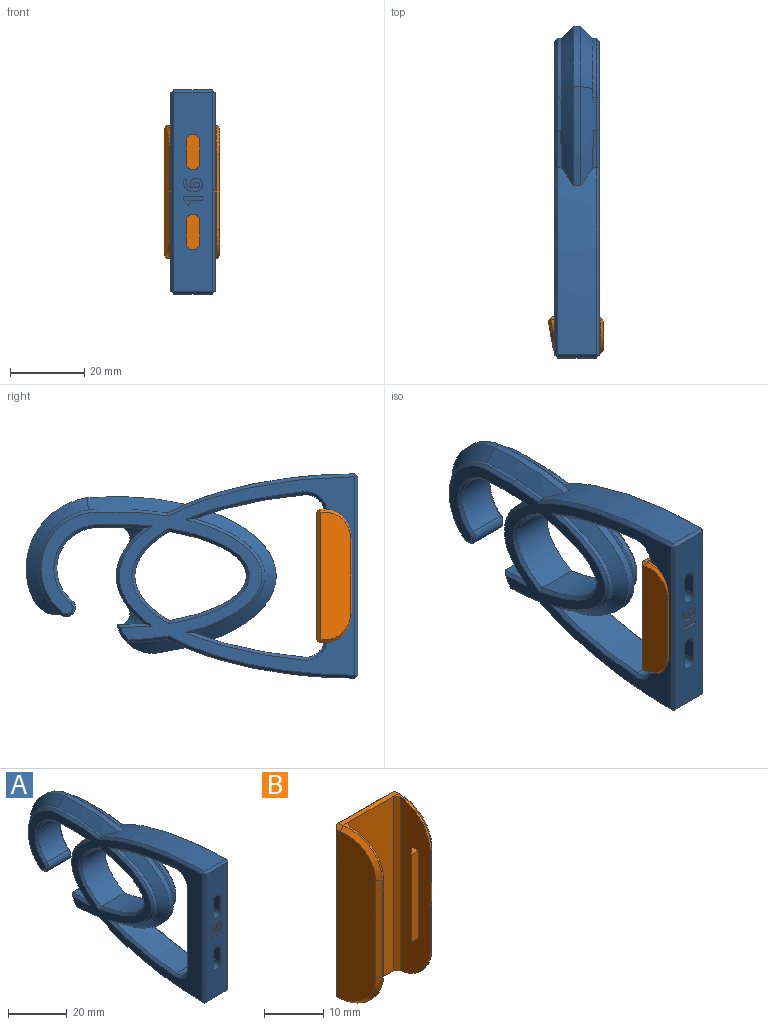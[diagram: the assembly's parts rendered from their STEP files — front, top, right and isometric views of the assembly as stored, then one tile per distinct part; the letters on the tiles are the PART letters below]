
ASSEMBLY  parts=2 mates=1
PART A: 167 faces, bbox 13x92.1x56.1 mm
  f0: plane 53.4x10.4mm, normal (0,-1,0), area 475.3mm2, adj f27,f28,f29,f30,f31,f32,f33,f34
  f1: cylinder r=16mm len=28.43mm, axis (-1,0,0), area 47.1mm2, adj f11,f13,f65,f66,f70,f76,f105
  f2: extruded ~10.08x1.04mm, area 9.1mm2, adj f13,f15,f70,f101
  f3: extruded ~10.91x4.2mm, area 19mm2, adj f16,f18,f62,f63,f100
  f4: extruded ~30.7x18.87mm, area 61.6mm2, adj f7,f10,f48,f114
  f5: plane 33.72x10.4mm, normal (0,1,0), area 111.2mm2, adj f8,f9,f35,f37,f38,f39,f40,f41
  f6: extruded ~24x11.2mm, area 354.4mm2, adj f24,f25,f122
  f7: extruded ~29.4x10.4mm, area 288mm2, adj f4,f8,f22,f47,f48,f49,f115,f119
  f8: cylinder r=5mm len=10.4mm, axis (-1,0,0), area 81.4mm2, adj f5,f7,f43,f113,f121
  f9: cylinder r=5mm len=10.4mm, axis (-1,0,0), area 81.4mm2, adj f5,f10,f36,f110,f118
  f10: extruded ~29.4x10.4mm, area 288mm2, adj f4,f9,f22,f47,f48,f49,f112,f116
  f11: cylinder r=2.5mm len=10.4mm, axis (-1,0,0), area 81.7mm2, adj f1,f12,f23,f72,f81,f107
  f12: cylinder r=16mm len=28.43mm, axis (-1,0,0), area 47.1mm2, adj f11,f13,f67,f68,f71,f77,f83
  f13: plane 10.41x8.77mm, normal (0,0,1), area 80.5mm2, adj f1,f2,f12,f14,f70,f71,f75,f85
  f14: extruded ~10.08x1.04mm, area 9.1mm2, adj f13,f15,f71,f87
  f15: extruded ~50.36x10.53mm, area 511.9mm2, adj f2,f14,f69,f70,f71,f90,f95,f99
  f16: extruded ~50.36x10.53mm, area 511.8mm2, adj f3,f17,f60,f62,f64,f88,f93,f98
  f17: extruded ~10.91x4.2mm, area 19mm2, adj f16,f18,f60,f61,f86
  f18: cylinder r=9.71mm len=10.76mm, axis (-1,0,0), area 76.6mm2, adj f3,f17,f19,f61,f63,f64,f84,f102
  f19: extruded ~10.4x7.29mm, area 38.9mm2, adj f18,f20,f55,f56,f57,f58,f59,f82
  f20: extruded ~25.66x10.4mm, area 250.9mm2, adj f19,f21,f50,f51,f52,f53,f54,f55
  f21: extruded ~13.86x10.4mm, area 107.3mm2, adj f20,f23,f50,f51,f52,f53,f54,f78
  f22: extruded ~30.7x18.87mm, area 61.6mm2, adj f7,f10,f47,f117
  f23: cylinder r=11mm len=19.46mm, axis (-1,0,0), area 267.4mm2, adj f11,f21,f79,f109
  f24: extruded ~24x20.76mm, area 570.7mm2, adj f6,f25,f123
  f25: plane 85.41x54.41mm, normal (1,0,0), area 1216.5mm2, adj f6,f24,f94,f98,f99,f100,f101,f102
  f26: plane 85.41x54.41mm, normal (-1,0,0), area 1177.9mm2, adj f78,f79,f80,f81,f82,f83,f84,f85
  f27: cylinder r=1.75mm len=6mm, axis (0,-1,0), area 33mm2, adj f0,f28,f30,f44
  f28: plane 6x6mm, normal (1,0,0), area 36mm2, adj f0,f27,f29,f42
  f29: cylinder r=1.75mm len=6mm, axis (0,-1,0), area 33mm2, adj f0,f28,f30,f41,f43,f45
  f30: plane 6x6mm, normal (-1,0,0), area 36mm2, adj f0,f27,f29,f46
  f31: plane 6x6mm, normal (-1,0,0), area 36mm2, adj f0,f32,f34,f40
  f32: cylinder r=1.75mm len=6mm, axis (0,-1,0), area 33mm2, adj f0,f31,f33,f35,f36,f38
  f33: plane 6x6mm, normal (1,0,0), area 36mm2, adj f0,f32,f34,f37
  f34: cylinder r=1.75mm len=6mm, axis (0,-1,0), area 33mm2, adj f0,f31,f33,f39
  f35: cone r=4.75mm half-angle=45deg, axis (0,1,0), area 9.8mm2, adj f5,f32,f36,f37
  f36: bspline ~7.18x3.11mm, area 20.9mm2, adj f9,f32,f35,f38
  f37: plane 6x3mm, normal (0.71,0.71,0), area 25.5mm2, adj f5,f33,f35,f39
  f38: cone r=4.75mm half-angle=45deg, axis (0,1,0), area 9.8mm2, adj f5,f32,f36,f40
  f39: cone r=4.75mm half-angle=45deg, axis (0,1,0), area 43.3mm2, adj f5,f34,f37,f40
  f40: plane 6x3mm, normal (-0.71,0.71,0), area 25.5mm2, adj f5,f31,f38,f39
  f41: cone r=4.75mm half-angle=45deg, axis (0,1,0), area 9.8mm2, adj f5,f29,f42,f43
  f42: plane 6x3mm, normal (0.71,0.71,0), area 25.5mm2, adj f5,f28,f41,f44
  f43: bspline ~7.18x3.11mm, area 20.9mm2, adj f8,f29,f41,f45
  f44: cone r=4.75mm half-angle=45deg, axis (0,1,0), area 43.3mm2, adj f5,f27,f42,f46
  f45: cone r=4.75mm half-angle=45deg, axis (0,1,0), area 9.8mm2, adj f5,f29,f43,f46
  f46: plane 6x3mm, normal (-0.71,0.71,0), area 25.5mm2, adj f5,f30,f44,f45
  f47: bspline ~40.67x32.57mm, area 230mm2, adj f7,f10,f22,f49
  f48: bspline ~40.67x32.57mm, area 230mm2, adj f4,f7,f10,f49
  f49: extruded ~34.16x17.06mm, area 102.3mm2, adj f7,f10,f47,f48
  f50: cone r=3mm half-angle=45deg, axis (1,0,0), area 12.9mm2, adj f20,f21,f51,f54
  f51: plane 0.41x0.27mm, normal (1,0,0), area 0.1mm2, adj f20,f21,f50
  f52: cone r=7mm half-angle=45deg, axis (-1,0,0), area 12.9mm2, adj f20,f21,f53,f54
  f53: plane 0.41x0.27mm, normal (-1,0,0), area 0.1mm2, adj f20,f21,f52
  f54: cylinder r=3mm len=4.8mm, axis (-1,0,0), area 13.2mm2, adj f20,f21,f50,f52
  f55: cone r=3mm half-angle=45deg, axis (1,0,0), area 12.9mm2, adj f19,f20,f56,f59
  f56: plane 0.41x0.27mm, normal (1,0,0), area 0.1mm2, adj f19,f20,f55
  f57: cone r=7mm half-angle=45deg, axis (-1,0,0), area 12.9mm2, adj f19,f20,f58,f59
  f58: plane 0.41x0.27mm, normal (-1,0,0), area 0.1mm2, adj f19,f20,f57
  f59: cylinder r=3mm len=4.8mm, axis (-1,0,0), area 13.2mm2, adj f19,f20,f55,f57
  f60: bspline ~14.46x6.99mm, area 25.7mm2, adj f16,f17,f61,f64
  f61: cone r=9.71mm half-angle=45deg, axis (1,0,0), area 18.1mm2, adj f17,f18,f60
  f62: bspline ~14.46x6.99mm, area 25.7mm2, adj f3,f16,f63,f64
  f63: cone r=5.71mm half-angle=45deg, axis (-1,0,0), area 18.1mm2, adj f3,f18,f62
  f64: extruded ~7.7x2mm, area 15.7mm2, adj f16,f18,f60,f62
  f65: cone r=15.27mm half-angle=45deg, axis (-1,0,0), area 153mm2, adj f1,f66,f70,f74
  f66: cone r=3mm half-angle=45deg, axis (-1,0,0), area 22.6mm2, adj f1,f65,f73,f76
  f67: cone r=19.27mm half-angle=45deg, axis (1,0,0), area 153mm2, adj f12,f68,f71,f74
  f68: cone r=7mm half-angle=45deg, axis (1,0,0), area 22.6mm2, adj f12,f67,f73,f77
  f69: extruded ~26.57x2.12mm, area 53.5mm2, adj f15,f70,f71,f74
  f70: bspline ~38.15x7.96mm, area 112.2mm2, adj f1,f2,f13,f15,f65,f69,f75
  f71: bspline ~38.15x7.96mm, area 112.2mm2, adj f12,f13,f14,f15,f67,f69,f75
  f72: plane 2x0.93mm, normal (0,0,-1), area 1.9mm2, adj f11,f73,f76,f77
  f73: cylinder r=7mm len=6.28mm, axis (-1,0,0), area 15.6mm2, adj f66,f68,f72,f74
  f74: cylinder r=19.27mm len=27.58mm, axis (-1,0,0), area 72.4mm2, adj f65,f67,f69,f73
  f75: extruded ~8.66x7.52mm, area 65.2mm2, adj f13,f70,f71
  f76: plane 0.95x0.83mm, normal (0.71,0,-0.71), area 0.5mm2, adj f1,f66,f72
  f77: plane 0.95x0.83mm, normal (-0.71,0,-0.71), area 0.5mm2, adj f12,f68,f72
  f78: bspline ~16.07x1.3mm, area 16.9mm2, adj f21,f26,f79,f80
  f79: cone r=11.8mm half-angle=45deg, axis (-1,0,0), area 30.2mm2, adj f23,f26,f78,f81
  f80: bspline ~30.07x11.02mm, area 36.3mm2, adj f20,f26,f78,f82
  f81: cone r=2.5mm half-angle=45deg, axis (1,0,0), area 7.5mm2, adj f11,f26,f79,f83
  f82: bspline ~10.35x1.36mm, area 8.9mm2, adj f19,f26,f80,f84
  f83: cone r=16mm half-angle=45deg, axis (1,0,0), area 43.4mm2, adj f12,f26,f81,f85
  f84: cone r=9.71mm half-angle=45deg, axis (1,0,0), area 5.4mm2, adj f18,f26,f82,f86
  f85: plane 8.76x0.8mm, normal (-0.71,0,0.71), area 9.9mm2, adj f13,f26,f83,f87
  f86: bspline ~11.21x1.9mm, area 12.3mm2, adj f17,f26,f84,f88
  f87: bspline ~10.39x1.87mm, area 11.6mm2, adj f14,f26,f85,f90
  f88: bspline ~55.49x12.73mm, area 58.6mm2, adj f16,f26,f86,f91
  f89: plane 53.4x0.8mm, normal (-0.71,-0.71,0), area 60.4mm2, adj f0,f26,f91,f92
  f90: bspline ~55.49x12.73mm, area 58.6mm2, adj f15,f26,f87,f92
  f91: plane 0.8x0.8mm, normal (-0.58,-0.58,-0.58), area 0.6mm2, adj f88,f89,f93
  f92: plane 0.8x0.8mm, normal (-0.58,-0.58,0.58), area 0.6mm2, adj f89,f90,f95
  f93: plane 10.4x0.8mm, normal (0,-0.71,-0.71), area 11.8mm2, adj f0,f16,f91,f96
  f94: plane 53.4x0.8mm, normal (0.71,-0.71,0), area 60.4mm2, adj f0,f25,f96,f97
  f95: plane 10.4x0.8mm, normal (0,-0.71,0.71), area 11.8mm2, adj f0,f15,f92,f97
  f96: plane 0.8x0.8mm, normal (0.58,-0.58,-0.58), area 0.6mm2, adj f93,f94,f98
  f97: plane 0.8x0.8mm, normal (0.58,-0.58,0.58), area 0.6mm2, adj f94,f95,f99
  f98: bspline ~55.49x12.73mm, area 58.6mm2, adj f16,f25,f96,f100
  f99: bspline ~55.49x12.73mm, area 58.6mm2, adj f15,f25,f97,f101
  f100: bspline ~11.21x1.9mm, area 12.3mm2, adj f3,f25,f98,f102
  f101: bspline ~10.39x1.87mm, area 11.6mm2, adj f2,f25,f99,f103
  f102: cone r=8.91mm half-angle=45deg, axis (-1,0,0), area 5.4mm2, adj f18,f25,f100,f104
  f103: plane 8.76x0.8mm, normal (0.71,0,0.71), area 9.9mm2, adj f13,f25,f101,f105
  f104: bspline ~9.42x1.3mm, area 8.9mm2, adj f19,f25,f102,f106
  f105: cone r=15.2mm half-angle=45deg, axis (-1,0,0), area 43.4mm2, adj f1,f25,f103,f107
  f106: bspline ~30.07x11.02mm, area 36.3mm2, adj f20,f25,f104,f108
  f107: cone r=1.7mm half-angle=45deg, axis (-1,0,0), area 7.5mm2, adj f11,f25,f105,f109
  f108: bspline ~16.07x1.3mm, area 16.9mm2, adj f21,f25,f106,f109
  f109: cone r=11mm half-angle=45deg, axis (1,0,0), area 30.2mm2, adj f23,f25,f107,f108
  f110: cone r=5mm half-angle=45deg, axis (1,0,0), area 10.2mm2, adj f9,f25,f111,f112
  f111: plane 33.72x0.8mm, normal (0.71,0.71,0), area 38.1mm2, adj f5,f25,f110,f113
  f112: bspline ~31.88x8.19mm, area 35.6mm2, adj f10,f25,f110,f114
  f113: cone r=5.8mm half-angle=45deg, axis (1,0,0), area 10.2mm2, adj f8,f25,f111,f115
  f114: bspline ~31.9x21.32mm, area 60mm2, adj f4,f25,f112,f115
  f115: bspline ~33.39x8.89mm, area 35.7mm2, adj f7,f25,f113,f114
  f116: bspline ~33.36x8.88mm, area 35.6mm2, adj f10,f26,f117,f118
  f117: bspline ~33.07x23.99mm, area 60mm2, adj f22,f26,f116,f119
  f118: cone r=5.8mm half-angle=45deg, axis (-1,0,0), area 10.2mm2, adj f9,f26,f116,f120
  f119: bspline ~33.39x8.89mm, area 35.7mm2, adj f7,f26,f117,f121
  f120: plane 33.72x0.8mm, normal (-0.71,0.71,0), area 38.1mm2, adj f5,f26,f118,f121
  f121: cone r=5mm half-angle=45deg, axis (-1,0,0), area 10.2mm2, adj f8,f26,f119,f120
  f122: bspline ~27.31x11.74mm, area 37.1mm2, adj f6,f26,f123
  f123: bspline ~26.44x24.47mm, area 59.3mm2, adj f24,f26,f122
  f124: cylinder r=1mm len=2mm, axis (1,0,0), area 6.3mm2, adj f25,f125,f127,f128
  f125: plane 18x2mm, normal (0,1,0), area 36mm2, adj f25,f124,f126,f128
  f126: cylinder r=1mm len=2mm, axis (1,0,0), area 6.3mm2, adj f25,f125,f127,f128
  f127: plane 18x2mm, normal (0,-1,0), area 36mm2, adj f25,f124,f126,f128
  f128: plane 20x2mm, normal (1,0,0), area 39.1mm2, adj f124,f125,f126,f127
  f129: extruded ~0.6x0.52mm, area 0.4mm2, adj f130,f153,f154,f166
  f130: extruded ~0.6x0.54mm, area 0.4mm2, adj f129,f131,f154,f166
  f131: extruded ~0.68x0.6mm, area 0.4mm2, adj f130,f132,f154,f166
  f132: extruded ~0.6x0.48mm, area 0.3mm2, adj f131,f133,f154,f166
  f133: extruded ~0.6x0.54mm, area 0.4mm2, adj f132,f134,f154,f166
  f134: extruded ~0.6x0.51mm, area 0.3mm2, adj f133,f135,f154,f166
  f135: extruded ~0.6x0.57mm, area 0.4mm2, adj f134,f153,f154,f166
  f136: extruded ~2.19x0.62mm, area 1.4mm2, adj f0,f137,f152,f154
  f137: extruded ~1.18x0.6mm, area 0.7mm2, adj f0,f136,f138,f154
  f138: extruded ~0.74x0.63mm, area 0.6mm2, adj f0,f137,f139,f154
  f139: extruded ~0.96x0.6mm, area 0.6mm2, adj f0,f138,f140,f154
  f140: extruded ~1.24x0.6mm, area 0.8mm2, adj f0,f139,f141,f154
  f141: extruded ~1.26x0.6mm, area 0.8mm2, adj f0,f140,f142,f154
  f142: extruded ~1.15x0.6mm, area 0.7mm2, adj f0,f141,f143,f154
  f143: extruded ~1.04x0.6mm, area 0.7mm2, adj f0,f142,f144,f154
  f144: extruded ~1.08x0.6mm, area 0.8mm2, adj f0,f143,f145,f154
  f145: plane 0.6x0.04mm, normal (1,0,0), area 0mm2, adj f0,f144,f146,f154
  f146: extruded ~0.91x0.6mm, area 0.6mm2, adj f0,f145,f147,f154
  f147: extruded ~0.6x0.51mm, area 0.4mm2, adj f0,f146,f148,f154
  f148: extruded ~0.88x0.6mm, area 0.5mm2, adj f0,f147,f149,f154
  f149: extruded ~0.6x0.6mm, area 0.4mm2, adj f0,f148,f150,f154
  f150: plane 0.84x0.6mm, normal (0,0,-1), area 0.5mm2, adj f0,f149,f151,f154
  f151: extruded ~0.66x0.6mm, area 0.4mm2, adj f0,f150,f152,f154
  f152: extruded ~1.86x0.72mm, area 1.2mm2, adj f0,f136,f151,f154
  f153: extruded ~0.64x0.6mm, area 0.4mm2, adj f129,f135,f154,f166
  f154: plane 5.08x3.5mm, normal (0,-1,0), area 10.5mm2, adj f129,f130,f131,f132,f133,f134,f135,f136
  f155: plane 1.05x0.6mm, normal (-1,0,0), area 0.6mm2, adj f0,f156,f164,f165
  f156: plane 4.96x0.6mm, normal (0,0,-1), area 3mm2, adj f0,f155,f157,f165
  f157: plane 0.86x0.6mm, normal (1,0,0), area 0.5mm2, adj f0,f156,f158,f165
  f158: plane 1.6x1.27mm, normal (0.78,0,0.62), area 1.2mm2, adj f0,f157,f159,f165
  f159: plane 0.63x0.6mm, normal (-0.63,0,0.78), area 0.5mm2, adj f0,f158,f160,f165
  f160: plane 0.6x0.57mm, normal (-0.78,0,-0.63), area 0.4mm2, adj f0,f159,f161,f165
  f161: extruded ~0.6x0.36mm, area 0.3mm2, adj f0,f160,f162,f165
  f162: plane 0.6x0.52mm, normal (0.03,0,1), area 0.3mm2, adj f0,f161,f163,f165
  f163: plane 0.6x0.47mm, normal (0.02,0,1), area 0.3mm2, adj f0,f162,f164,f165
  f164: plane 2.87x0.6mm, normal (0,0,1), area 1.7mm2, adj f0,f155,f163,f165
  f165: plane 4.96x2.46mm, normal (0,-1,0), area 6.4mm2, adj f155,f156,f157,f158,f159,f160,f161,f162
  f166: plane 1.65x1.45mm, normal (0,-1,0), area 1.9mm2, adj f129,f130,f131,f132,f133,f134,f135,f153
PART B: 35 faces, bbox 14.9x9.8x36 mm
  f0: plane 35.92x7.2mm, normal (-1,0,0), area 204.8mm2, adj f1,f10,f11,f12,f13,f14,f15,f34
  f1: plane 20x0.4mm, normal (0,-1,0), area 8mm2, adj f0,f14,f15,f24
  f2: plane 13.38x1.07mm, normal (0,0,-1), area 13.3mm2, adj f8,f15,f16,f28,f30,f32
  f3: plane 20x0.39mm, normal (0.17,-0.98,0), area 8mm2, adj f7,f16,f17,f29
  f4: plane 13.38x1.07mm, normal (0,0,1), area 13.3mm2, adj f8,f14,f17,f21,f23,f25
  f5: plane 34.4x7.99mm, normal (-0.98,-0.17,0), area 256.8mm2, adj f19,f25,f27,f29,f31,f32
  f6: plane 34.4x7.8mm, normal (1,0,0), area 246.1mm2, adj f20,f21,f22,f24,f26,f28
  f7: plane 35.89x6.94mm, normal (0.98,0.17,0), area 226.2mm2, adj f3,f16,f17,f33
  f8: plane 36x11.6mm, normal (0,-1,0), area 383.3mm2, adj f2,f4,f16,f17,f33,f34
  f9: plane 34.4x12.63mm, normal (0,1,0), area 434.5mm2, adj f19,f20,f23,f30
  f10: plane 18x0.3mm, normal (0,1,0), area 5.4mm2, adj f0,f11,f13,f18
  f11: plane 1.8x1.5mm, normal (0,0,1), area 1.6mm2, adj f0,f10,f12,f18
  f12: plane 18x1.8mm, normal (0,-1,0), area 32.4mm2, adj f0,f11,f13,f18
  f13: plane 1.8x1.5mm, normal (0,0,-1), area 1.6mm2, adj f0,f10,f12,f18
  f14: cylinder r=8mm len=8mm, axis (1,0,0), area 5.3mm2, adj f0,f1,f4,f22,f34
  f15: cylinder r=8mm len=8mm, axis (-1,0,0), area 5.3mm2, adj f0,f1,f2,f26,f34
  f16: cylinder r=8mm len=8.11mm, axis (-0.98,-0.17,0), area 5.5mm2, adj f2,f3,f7,f8,f31,f33
  f17: cylinder r=8mm len=8.11mm, axis (0.98,0.17,0), area 5.5mm2, adj f3,f4,f7,f8,f27,f33
  f18: plane 18x1.5mm, normal (-0.71,0.71,0), area 38.2mm2, adj f10,f11,f12,f13
  f19: plane 35.59x1.11mm, normal (-0.71,0.71,0), area 54.9mm2, adj f5,f9,f23,f25,f30,f32
  f20: plane 35.6x1.2mm, normal (0.71,0.71,0), area 59.4mm2, adj f6,f9,f21,f23,f28,f30
  f21: plane 1.2x0.8mm, normal (0.71,0,0.71), area 1.1mm2, adj f4,f6,f20,f22,f23
  f22: cone r=7.2mm half-angle=45deg, axis (-1,0,0), area 13.5mm2, adj f6,f14,f21,f24
  f23: plane 13.83x0.8mm, normal (0,0.71,0.71), area 15.1mm2, adj f4,f9,f19,f20,f21,f25
  f24: plane 20x0.8mm, normal (0.71,-0.71,0), area 22.6mm2, adj f1,f6,f22,f26
  f25: plane 1.41x0.95mm, normal (-0.7,-0.12,0.71), area 1.3mm2, adj f4,f5,f19,f23,f27
  f26: cone r=7.2mm half-angle=45deg, axis (-1,0,0), area 13.5mm2, adj f6,f15,f24,f28
  f27: cone r=7.2mm half-angle=45deg, axis (0.98,0.17,0), area 13.5mm2, adj f5,f17,f25,f29
  f28: plane 1.2x0.8mm, normal (0.71,0,-0.71), area 1.1mm2, adj f2,f6,f20,f26,f30
  f29: plane 20x0.93mm, normal (-0.57,-0.82,0), area 22.6mm2, adj f3,f5,f27,f31
  f30: plane 13.83x0.8mm, normal (0,0.71,-0.71), area 15.1mm2, adj f2,f9,f19,f20,f28,f32
  f31: cone r=7.2mm half-angle=45deg, axis (0.98,0.17,0), area 13.5mm2, adj f5,f16,f29,f32
  f32: plane 1.41x0.95mm, normal (-0.7,-0.12,-0.71), area 1.3mm2, adj f2,f5,f19,f30,f31
  f33: plane 36x0.94mm, normal (0.77,-0.64,0), area 44.1mm2, adj f7,f8,f16,f17
  f34: plane 36x0.8mm, normal (-0.71,-0.71,0), area 40.7mm2, adj f0,f8,f14,f15
PLACE A at identity
PLACE B t=(0,-105.11,-2.5)mm
MATE planar B.f0 <-> A.f25  axis (-1,0,0) through (6,-134.5,-2.5)mm
